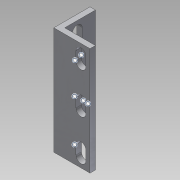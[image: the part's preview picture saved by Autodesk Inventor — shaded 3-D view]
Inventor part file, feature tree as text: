
AUTODESK INVENTOR PART (.ipt)
format: ipt  version: 2013 SP2 (Build 170200200, 200)  size: 151,552 bytes
history: native  units: mm
features: extrude x3, sketch x3, pattern_linear x1
ambient origin geometry x8: Origin, YZ Plane, XZ Plane, XY Plane, X Axis, Y Axis, Z Axis, Center Point
bodies: Solid1 (feature_tree)
feature tree (7):
  extrude  "Extrusion1"  Depth=3.0mm
  extrude  "Extrusion2"  Depth=17.0mm
  extrude  "Extrusion3"  Depth=5.5mm
  pattern_linear  "Rectangular Pattern1"  Spacing1=2.75mm  [1 undecoded]
  sketch  "Sketch1"  dims[d0=20.0mm d1=3.0mm]
  sketch  "Sketch2"  dims[d2=17.0mm d3=17.0mm]
  sketch  "Sketch3"  dims[d5=0.0mm d7=5.5mm d10=2.75mm d11=14.5mm d12=0.0mm d14=10.5mm d15=5.5mm d16=2.75mm d17=2.05mm d18=14.5mm d19=0.0mm d23=0.0mm d24=0.0mm d25=0.0mm d26=0.0mm d27=0.0mm d28=0.0mm d29=0.0mm d30=0.0mm d31=0.0mm d32=0.0mm d33=0.0mm d34=0.0mm]
note: 1 required parameter value undecoded (feature->parameter linkage not recoverable at this tier; creation-order binding heuristic only, values carry confidence <= 0.55)
